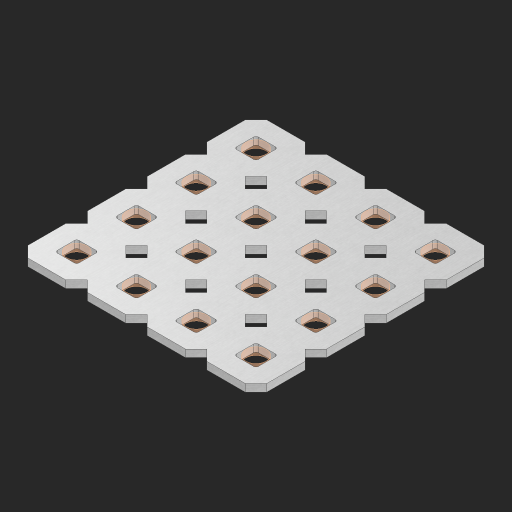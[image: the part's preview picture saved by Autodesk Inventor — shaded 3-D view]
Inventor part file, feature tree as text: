
AUTODESK INVENTOR PART (.ipt)
format: ipt  version: 2023 (Build 270158000, 158)  size: 483,840 bytes
history: native  units: in
note: dims shown in document units (in); Inventor stores cm internally (conversion verified against a paired STEP export)
features: other x17, extrude x15, sketch x2, pattern_linear x1
ambient origin geometry x8: Origin, YZ Plane, XZ Plane, XY Plane, X Axis, Y Axis, Z Axis, Center Point
bodies: Solid1 (feature_tree), Body (feature_tree)
feature tree (35):
  pattern_linear  "Rectangular Pattern1"  Spacing1=0.09in  [1 undecoded]
  sketch  "Sketch1"  dims[d1=0.5in]
  sketch  "Sketch2"  dims[d2=0.182in d3=0.09in d4=0.09in d5=0.09in d6=0.09in d7=0.09in d8=0.09in d9=0.09in d10=0.09in d11=0.02in d13=0.0in d14=0.172in d15=0.0625in d16=0.0in d19=0.5in d22=0.5in]
  other  "Srf1"
  other  "Srf126"
  other  "Srf127"
  other  "Srf128"
  other  "Srf268"
  other  "Srf269"
  other  "Srf270"
  other  "Srf271"
  other  "Srf293"
  other  "Srf294"
  other  "Srf295"
  other  "Srf296"
  other  "Srf318"
  other  "Srf319"
  other  "Srf320"
  other  "Srf321"
  other  "Circle"
  extrude  "ExtrusionSrf126"  Depth=0.09in
  extrude  "ExtrusionSrf127"  Depth=0.09in
  extrude  "ExtrusionSrf128"  Depth=0.09in
  extrude  "ExtrusionSrf268"  Depth=0.09in
  extrude  "ExtrusionSrf269"  Depth=0.09in
  extrude  "ExtrusionSrf270"  Depth=0.09in
  extrude  "ExtrusionSrf271"  Depth=0.09in
  extrude  "ExtrusionSrf293"  Depth=0.02in
  extrude  "ExtrusionSrf294"  TaperAngle=0.0deg  [1 undecoded]
  extrude  "ExtrusionSrf295"  Depth=0.5in
  extrude  "ExtrusionSrf296"  Depth=0.0625in TaperAngle=0.0deg
  extrude  "ExtrusionSrf318"  Depth=0.5in
  extrude  "ExtrusionSrf319"  Depth=0.5in
  extrude  "ExtrusionSrf320"  [1 undecoded]
  extrude  "ExtrusionSrf321"  [1 undecoded]
note: 4 required parameter values undecoded (feature->parameter linkage not recoverable at this tier; creation-order binding heuristic only, values carry confidence <= 0.55)
